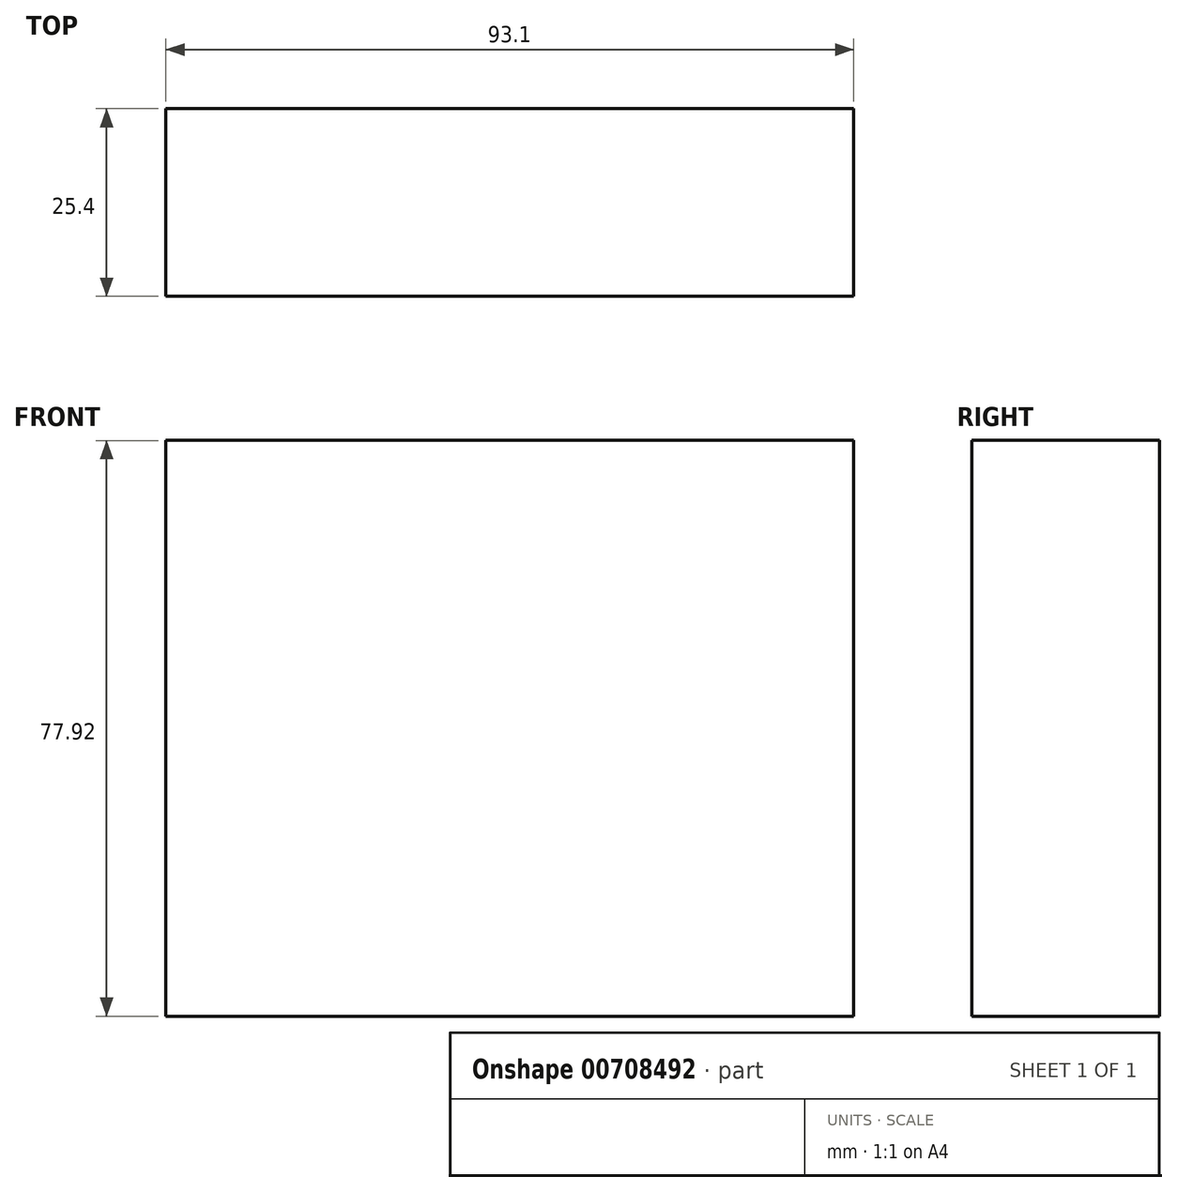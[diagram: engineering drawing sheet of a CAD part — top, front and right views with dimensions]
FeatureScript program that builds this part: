
annotation { "Feature Type Name" : "Feature", "Feature Type Description" : "" }
export const myFeature = defineFeature(function(context is Context, id is Id, definition is map)
    precondition{}
    {
        {
            var Q0;
            Q0=qCreatedBy(makeId("Front.planeOp"),FACE);
            var sketch = newSketch(context, id + "F0", { "sketchPlane" : qUnion([Q0])});
            skLineSegment(sketch, "E0.bottom", {"start": v(-46.55, 38.96) * mm, "end": v(46.55, 38.96) * mm});
            skLineSegment(sketch, "E0.top", {"start": v(-46.55, -38.96) * mm, "end": v(46.55, -38.96) * mm});
            skLineSegment(sketch, "E0.left", {"start": v(-46.55, 38.96) * mm, "end": v(-46.55, -38.96) * mm});
            skLineSegment(sketch, "E0.right", {"start": v(46.55, 38.96) * mm, "end": v(46.55, -38.96) * mm});
            skPoint(sketch, "E0.middle", {"position": v(0, 0) * mm});
            skSolve(sketch);
        }
        {
            var Q0;
            Q0=makeQuery(id+"F0.imprint","IMPRINT",FACE,{"disambiguationData":[TD([[makeQuery(id+"F0.imprint","IMPRINT",EDGE,{"derivedFrom":sQuery(id+"F0.wireOp",EDGE,"E0.bottom")}),-1.0]])]});
            extrude(context, id + "F1", {"entities" : qUnion([Q0]), "endBound" : BoundingType.SYMMETRIC, "depth" : 25.4 * mm, "offsetDistance" : 25.4 * mm});
        }
    });
